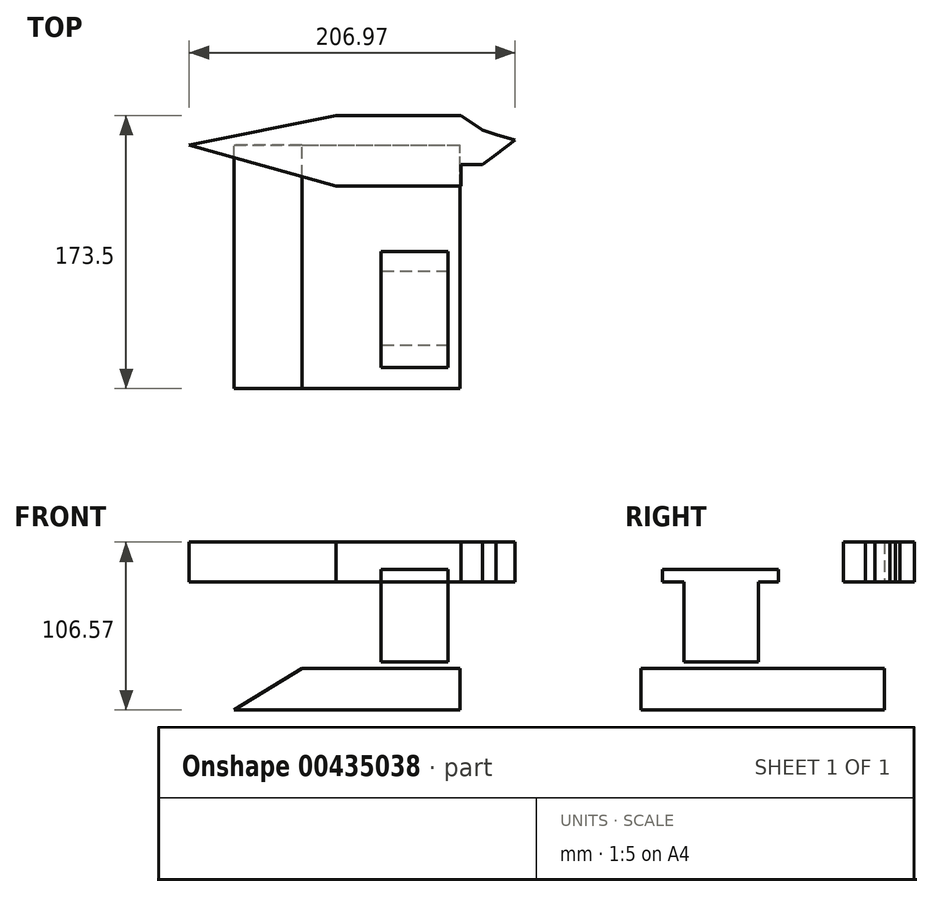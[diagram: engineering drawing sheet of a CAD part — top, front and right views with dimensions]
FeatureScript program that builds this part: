
annotation { "Feature Type Name" : "Feature", "Feature Type Description" : "" }
export const myFeature = defineFeature(function(context is Context, id is Id, definition is map)
    precondition{}
    {
        {
            var Q0;
            Q0=qCreatedBy(makeId("Top.planeOp"),FACE);
            var sketch = newSketch(context, id + "F0", { "sketchPlane" : qUnion([Q0])});
            skLineSegment(sketch, "E0.bottom", {"start": v(-28.74, 18.83) * mm, "end": v(50.8, 18.83) * mm});
            skLineSegment(sketch, "E0.top", {"start": v(-28.74, -26.07) * mm, "end": v(50.8, -26.07) * mm});
            skLineSegment(sketch, "E0.left", {"start": v(-28.74, 18.83) * mm, "end": v(-28.74, -26.07) * mm});
            skLineSegment(sketch, "E0.right", {"start": v(50.8, 18.83) * mm, "end": v(50.8, -26.07) * mm});
            skLineSegment(sketch, "E1", {"start": v(-28.74, 18.83) * mm, "end": v(-121.83, 0) * mm});
            skLineSegment(sketch, "E2", {"start": v(-121.83, 0) * mm, "end": v(-28.74, -26.07) * mm});
            skLineSegment(sketch, "E3", {"start": v(50.8, 9.64) * mm, "end": v(64.45, 9.64) * mm});
            skLineSegment(sketch, "E4", {"start": v(64.45, 9.64) * mm, "end": v(64.45, -12.2) * mm});
            skLineSegment(sketch, "E5", {"start": v(64.45, -12.2) * mm, "end": v(50.8, -12.2) * mm});
            skLineSegment(sketch, "E6", {"start": v(50.8, -12.2) * mm, "end": v(64.45, -12.2) * mm});
            skLineSegment(sketch, "E7", {"start": v(64.45, 0) * mm, "end": v(64.45, 9.64) * mm});
            skLineSegment(sketch, "E8", {"start": v(64.45, -12.2) * mm, "end": v(73.13, 0) * mm});
            skLineSegment(sketch, "E9", {"start": v(73.13, 0) * mm, "end": v(73.13, -6.1) * mm});
            skPoint(sketch, "E9.endSnap0", {"position": v(68.79, -6.1) * mm});
            skLineSegment(sketch, "E10", {"start": v(73.13, -6.1) * mm, "end": v(68.79, -6.1) * mm});
            skLineSegment(sketch, "E11", {"start": v(73.13, 0) * mm, "end": v(73.13, 6.75) * mm});
            skLineSegment(sketch, "E12", {"start": v(73.13, 6.75) * mm, "end": v(64.45, 9.64) * mm});
            skLineSegment(sketch, "E13", {"start": v(73.13, 0) * mm, "end": v(85.14, 3.38) * mm});
            skPoint(sketch, "E13.endSnap0", {"position": v(73.13, 3.38) * mm});
            skLineSegment(sketch, "E14", {"start": v(85.14, 3.38) * mm, "end": v(73.13, 6.75) * mm});
            skLineSegment(sketch, "E15", {"start": v(50.8, 18.83) * mm, "end": v(64.45, 9.64) * mm});
            skLineSegment(sketch, "E16", {"start": v(64.45, -12.2) * mm, "end": v(50.8, -26.07) * mm});
            skLineSegment(sketch, "E17", {"start": v(64.45, -12.2) * mm, "end": v(73.13, -6.1) * mm});
            skLineSegment(sketch, "E18", {"start": v(73.13, -6.1) * mm, "end": v(85.14, 3.38) * mm});
            skSolve(sketch);
        }
        {
            var Q0;
            {var subQ1=sQuery(id+"F0.wireOp",EDGE,"E0.bottom");Q0=makeQuery(id+"F0.imprint","IMPRINT",FACE,{"disambiguationData":[TD([[makeQuery(id+"F0.imprint","IMPRINT",EDGE,{"derivedFrom":subQ1}),-1.0]])]});}
            var Q1;
            Q1=makeQuery(id+"F0.imprint","IMPRINT",FACE,{"disambiguationData":[TD([[makeQuery(id+"F0.imprint","IMPRINT",EDGE,{"derivedFrom":sQuery(id+"F0.wireOp",EDGE,"E0.left")}),-1.0]])]});
            var Q2;
            {var subQ1=sQuery(id+"F0.wireOp",EDGE,"E3");Q2=makeQuery(id+"F0.imprint","IMPRINT",FACE,{"disambiguationData":[TD([[makeQuery(id+"F0.imprint","IMPRINT",EDGE,{"derivedFrom":subQ1}),-1.0]])]});}
            var Q3;
            {var subQ2=sQuery(id+"F0.wireOp",EDGE,"E6");Q3=makeQuery(id+"F0.imprint","IMPRINT",FACE,{"disambiguationData":[TD([[makeQuery(id+"F0.imprint","IMPRINT",EDGE,{"derivedFrom":subQ2}),-1.0]])]});}
            var Q4;
            {var subQ2=sQuery(id+"F0.wireOp",EDGE,"E3");Q4=makeQuery(id+"F0.imprint","IMPRINT",FACE,{"disambiguationData":[TD([[makeQuery(id+"F0.imprint","IMPRINT",EDGE,{"derivedFrom":subQ2}),1.0]])]});}
            var Q5;
            {var subQ3=sQuery(id+"F0.wireOp",EDGE,"E4");Q5=makeQuery(id+"F0.imprint","IMPRINT",FACE,{"disambiguationData":[TD([[makeQuery(id+"F0.imprint","IMPRINT",EDGE,{"derivedFrom":subQ3}),1.0]])]});}
            var Q6;
            {var subQ0=sQuery(id+"F0.wireOp",EDGE,"E9");Q6=makeQuery(id+"F0.imprint","IMPRINT",FACE,{"disambiguationData":[TD([[makeQuery(id+"F0.imprint","IMPRINT",EDGE,{"derivedFrom":subQ0}),-1.0]])]});}
            var Q7;
            {var subQ2=sQuery(id+"F0.wireOp",EDGE,"E10");Q7=makeQuery(id+"F0.imprint","IMPRINT",FACE,{"disambiguationData":[TD([[makeQuery(id+"F0.imprint","IMPRINT",EDGE,{"derivedFrom":subQ2}),1.0]])]});}
            var Q8;
            Q8=makeQuery(id+"F0.imprint","IMPRINT",FACE,{"disambiguationData":[TD([[makeQuery(id+"F0.imprint","IMPRINT",EDGE,{"derivedFrom":sQuery(id+"F0.wireOp",EDGE,"E9")}),1.0]])]});
            var Q9;
            Q9=makeQuery(id+"F0.imprint","IMPRINT",FACE,{"disambiguationData":[TD([[makeQuery(id+"F0.imprint","IMPRINT",EDGE,{"derivedFrom":sQuery(id+"F0.wireOp",EDGE,"E11")}),-1.0]])]});
            extrude(context, id + "F1", {"entities" : qUnion([Q0, Q1, Q2, Q3, Q4, Q5, Q6, Q7, Q8, Q9]), "depth" : 25.4 * mm});
        }
        {
            var Q0;
            Q0=qCreatedBy(makeId("Front.planeOp"),FACE);
            var sketch = newSketch(context, id + "F2", { "sketchPlane" : qUnion([Q0])});
            skLineSegment(sketch, "E19.bottom", {"start": v(22.99, 0) * mm, "end": v(-22.99, 0) * mm});
            skLineSegment(sketch, "E19.top", {"start": v(22.99, 0) * mm, "end": v(-22.99, 0) * mm});
            skLineSegment(sketch, "E19.left", {"start": v(22.99, 0) * mm, "end": v(22.99, 0) * mm});
            skLineSegment(sketch, "E19.right", {"start": v(-22.99, 0) * mm, "end": v(-22.99, 0) * mm});
            skPoint(sketch, "E19.middle", {"position": v(0, 0) * mm});
            skLineSegment(sketch, "E20.top", {"start": v(22.99, -68.02) * mm, "end": v(-22.99, -68.02) * mm});
            skLineSegment(sketch, "E20.left", {"start": v(22.99, 0) * mm, "end": v(22.99, -68.02) * mm});
            skLineSegment(sketch, "E20.right", {"start": v(-22.99, 0) * mm, "end": v(-22.99, -68.02) * mm});
            skPoint(sketch, "E20.middle", {"position": v(0, -34) * mm});
            skLineSegment(sketch, "E21.bottom", {"start": v(-50.23, -81.17) * mm, "end": v(50.23, -81.17) * mm});
            skLineSegment(sketch, "E21.top", {"start": v(-50.23, -54.86) * mm, "end": v(50.23, -54.86) * mm});
            skLineSegment(sketch, "E21.left", {"start": v(-50.23, -81.17) * mm, "end": v(-50.23, -54.86) * mm});
            skLineSegment(sketch, "E21.right", {"start": v(50.23, -81.17) * mm, "end": v(50.23, -54.86) * mm});
            skPoint(sketch, "E21.middle", {"position": v(0, -68.02) * mm});
            skLineSegment(sketch, "E22", {"start": v(-50.23, -54.86) * mm, "end": v(-93.24, -81.17) * mm});
            skLineSegment(sketch, "E23", {"start": v(-93.24, -81.17) * mm, "end": v(-50.23, -81.17) * mm});
            skLineSegment(sketch, "E24", {"start": v(50.14, -55.57) * mm, "end": v(78.9, -82.15) * mm});
            skLineSegment(sketch, "E25", {"start": v(78.9, -82.15) * mm, "end": v(50.23, -81.17) * mm});
            skSolve(sketch);
        }
        {
            var Q0;
            {var subQ1=sQuery(id+"F2.wireOp",EDGE,"E20.top");Q0=makeQuery(id+"F2.imprint","IMPRINT",FACE,{"disambiguationData":[TD([[makeQuery(id+"F2.imprint","IMPRINT",EDGE,{"derivedFrom":subQ1}),1.0]])]});}
            var Q1;
            Q1=makeQuery(id+"F2.imprint","IMPRINT",FACE,{"disambiguationData":[TD([[makeQuery(id+"F2.imprint","IMPRINT",EDGE,{"derivedFrom":sQuery(id+"F2.wireOp",EDGE,"E21.left")}),1.0]])]});
            var Q2;
            {var subQ0=sQuery(id+"F2.wireOp",EDGE,"E20.top");Q2=makeQuery(id+"F2.imprint","IMPRINT",FACE,{"disambiguationData":[TD([[makeQuery(id+"F2.imprint","IMPRINT",EDGE,{"derivedFrom":subQ0}),-1.0]])]});}
            extrude(context, id + "F3", {"entities" : qUnion([Q0, Q1, Q2]), "depth" : 154.67 * mm});
        }
        {
            var Q0;
            Q0=qCreatedBy(makeId("Right.planeOp"),FACE);
            var sketch = newSketch(context, id + "F4", { "sketchPlane" : qUnion([Q0])});
            skLineSegment(sketch, "E26.bottom", {"start": v(-80.2, 0) * mm, "end": v(-127.25, 0) * mm});
            skLineSegment(sketch, "E26.top", {"start": v(-80.2, -50.54) * mm, "end": v(-127.25, -50.54) * mm});
            skLineSegment(sketch, "E26.left", {"start": v(-80.2, 0) * mm, "end": v(-80.2, -50.54) * mm});
            skLineSegment(sketch, "E26.right", {"start": v(-127.25, 0) * mm, "end": v(-127.25, -50.54) * mm});
            skLineSegment(sketch, "E27.bottom", {"start": v(-67.47, 0) * mm, "end": v(-141.17, 0) * mm});
            skLineSegment(sketch, "E27.top", {"start": v(-67.47, 8.06) * mm, "end": v(-141.17, 8.06) * mm});
            skLineSegment(sketch, "E27.left", {"start": v(-67.47, 0) * mm, "end": v(-67.47, 8.06) * mm});
            skLineSegment(sketch, "E27.right", {"start": v(-141.17, 0) * mm, "end": v(-141.17, 8.06) * mm});
            skSolve(sketch);
        }
        {
            var Q0;
            Q0=makeQuery(id+"F4.imprint","IMPRINT",FACE,{"disambiguationData":[TD([[makeQuery(id+"F4.imprint","IMPRINT",EDGE,{"derivedFrom":sQuery(id+"F4.wireOp",EDGE,"E26.top")}),-1.0]])]});
            var Q1;
            Q1=makeQuery(id+"F4.imprint","IMPRINT",FACE,{"disambiguationData":[TD([[makeQuery(id+"F4.imprint","IMPRINT",EDGE,{"derivedFrom":sQuery(id+"F4.wireOp",EDGE,"E27.top")}),1.0]])]});
            extrude(context, id + "F5", {"entities" : qUnion([Q0, Q1]), "depth" : 42.62 * mm});
        }
    });
